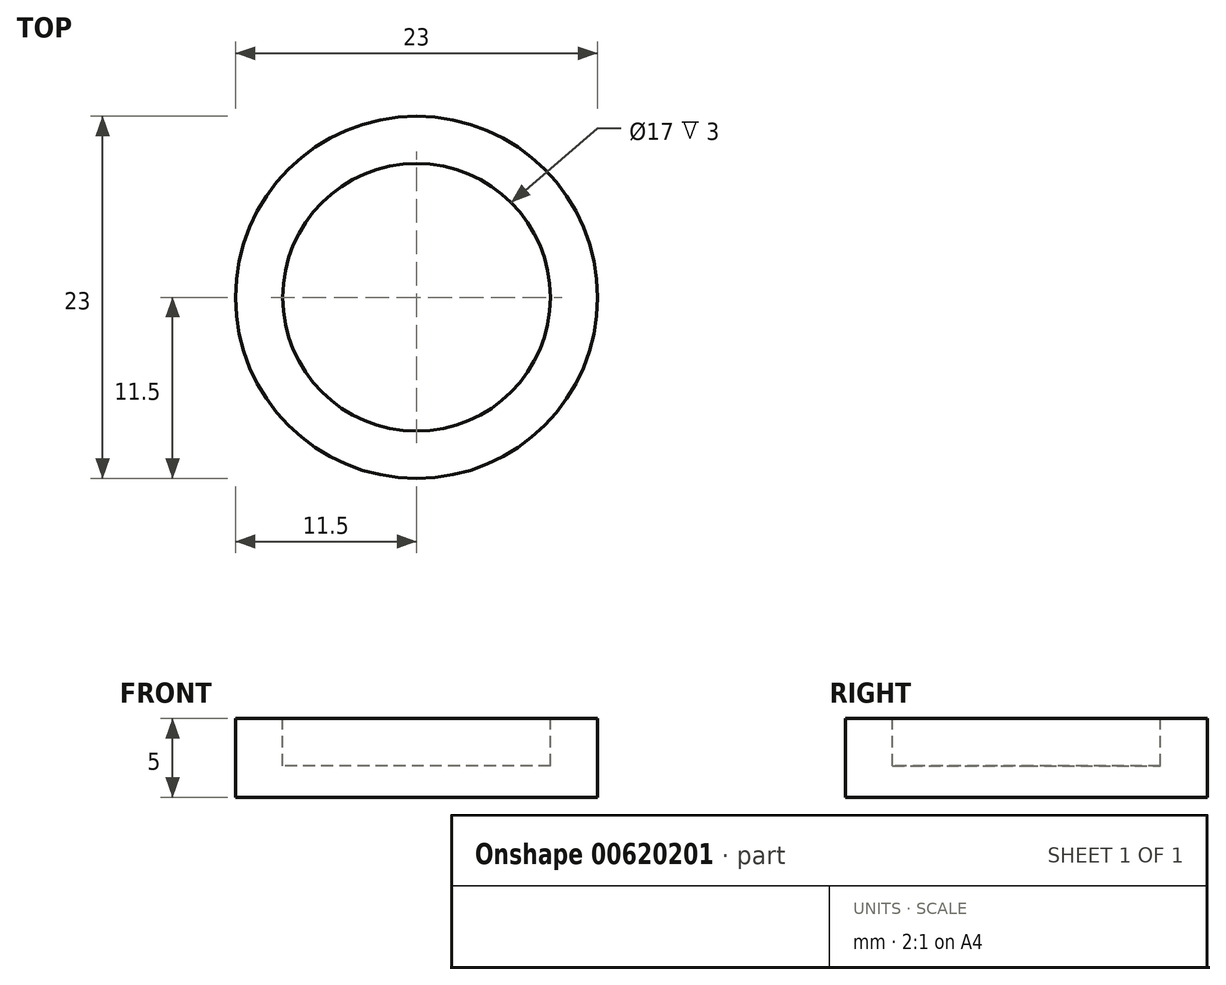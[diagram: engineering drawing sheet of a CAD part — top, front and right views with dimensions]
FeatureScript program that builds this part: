
annotation { "Feature Type Name" : "Feature", "Feature Type Description" : "" }
export const myFeature = defineFeature(function(context is Context, id is Id, definition is map)
    precondition{}
    {
        {
            var Q0;
            Q0=qCreatedBy(makeId("Top.planeOp"),FACE);
            var sketch = newSketch(context, id + "F0", { "sketchPlane" : qUnion([Q0])});
            skCircle(sketch, "E0", {"center": v(0, 0) * mm, "radius": 11.5 * mm});
            skSolve(sketch);
        }
        {
            var Q0;
            Q0=makeQuery(id+"F0.imprint","IMPRINT",FACE,{"disambiguationData":[TD([[makeQuery(id+"F0.imprint","IMPRINT",EDGE,{"derivedFrom":sQuery(id+"F0.wireOp",EDGE,"E0")}),1.0]])]});
            extrude(context, id + "F1", {"entities" : qUnion([Q0]), "oppositeDirection" : true, "depth" : 2 * mm, "offsetDistance" : 25 * mm});
        }
        {
            var Q0;
            Q0=makeQuery(id+"F1.opExtrude","CAP_FACE",FACE,{"disambiguationData":[OSD([sQuery(id+"F0.wireOp",EDGE,"E0")])],"isStart":true});
            var sketch = newSketch(context, id + "F2", { "sketchPlane" : qUnion([Q0])});
            skCircle(sketch, "E1", {"center": v(0, 0) * mm, "radius": 11.5 * mm});
            skSolve(sketch);
        }
        {
            var Q0;
            Q0 = qSketchRegion(id + "F2", true);
            extrude(context, id + "F3", {"entities" : qUnion([Q0]), "operationType" : NewBodyOperationType.ADD, "depth" : 3 * mm, "offsetDistance" : 25 * mm});
        }
        {
            var Q0;
            Q0=makeQuery(id+"F3.opExtrude","CAP_FACE",FACE,{"disambiguationData":[OSD([sQuery(id+"F2.wireOp",EDGE,"E1")])],"isStart":false});
            var sketch = newSketch(context, id + "F4", { "sketchPlane" : qUnion([Q0])});
            skCircle(sketch, "E2", {"center": v(0, 0) * mm, "radius": 8.5 * mm});
            skSolve(sketch);
        }
        {
            var Q0;
            Q0=makeQuery(id+"F4.imprint","IMPRINT",FACE,{"disambiguationData":[TD([[makeQuery(id+"F4.imprint","IMPRINT",EDGE,{"derivedFrom":sQuery(id+"F4.wireOp",EDGE,"E2")}),1.0]])]});
            extrude(context, id + "F5", {"entities" : qUnion([Q0]), "operationType" : NewBodyOperationType.REMOVE, "oppositeDirection" : true, "depth" : 3 * mm, "offsetDistance" : 25 * mm});
        }
    });
